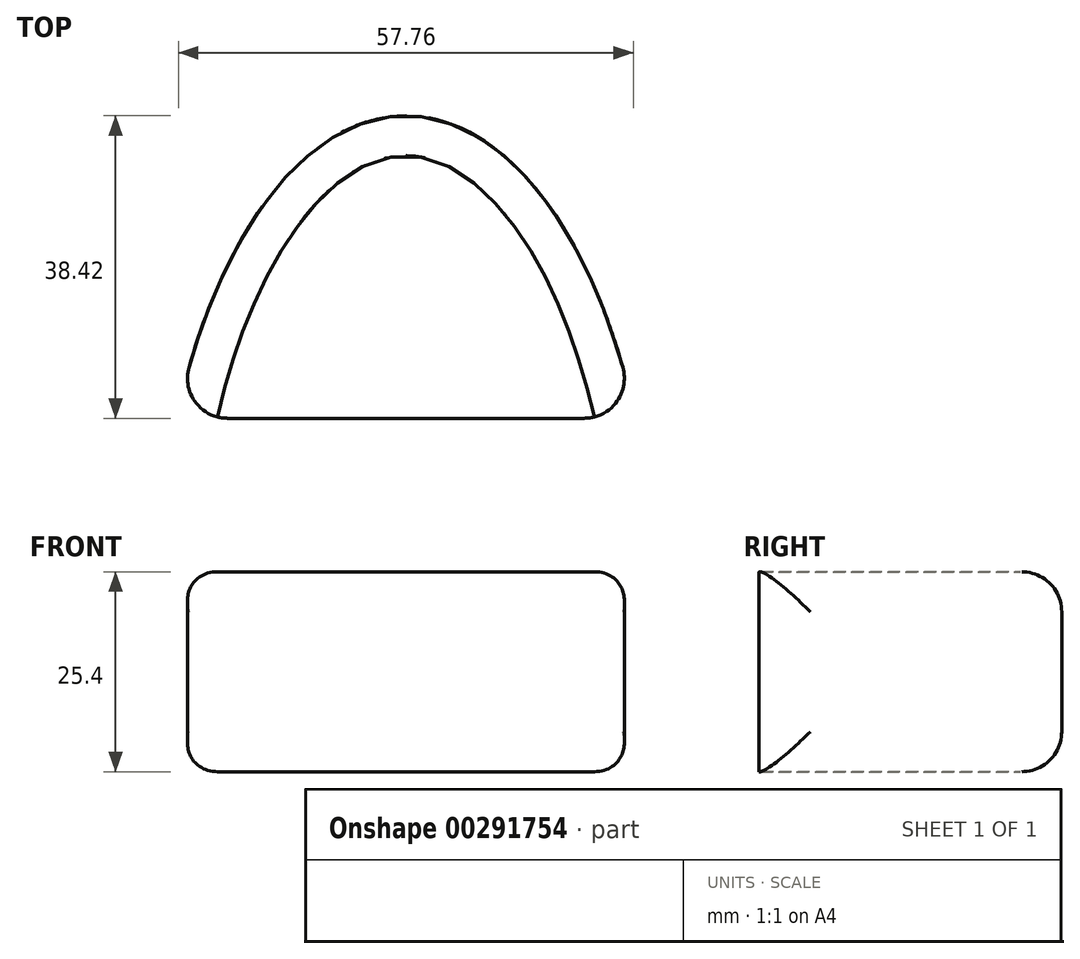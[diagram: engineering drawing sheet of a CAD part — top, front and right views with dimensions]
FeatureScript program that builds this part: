
annotation { "Feature Type Name" : "Feature", "Feature Type Description" : "" }
export const myFeature = defineFeature(function(context is Context, id is Id, definition is map)
    precondition{}
    {
        {
            var Q0;
            Q0=qCreatedBy(makeId("Top.planeOp"),FACE);
            var sketch = newSketch(context, id + "F0", { "sketchPlane" : qUnion([Q0])});
            skEllipticalArc(sketch, "E0", {});
            skFitSpline(sketch, "E1.0", {"points": [v(1.64, 55.77) * mm, v(0, 55.93) * mm, v(-1.64, 55.77) * mm, v(-3.37, 55.26) * mm, v(-5.25, 54.33) * mm, v(-7.27, 52.89) * mm, v(-9.39, 50.9) * mm, v(-11.52, 48.35) * mm, v(-13.28, 45.76) * mm, v(-14.64, 43.41) * mm, v(-15.64, 41.51) * mm, v(-16.6, 39.5) * mm, v(-17.82, 36.66) * mm, v(-19.22, 32.88) * mm, v(-20.69, 27.99) * mm, v(-21.91, 22.8) * mm, v(-22.89, 17.36) * mm, v(-23.6, 11.71) * mm, v(-23.96, 6.88) * mm, v(-24.1, 2.96) * mm, v(-24.14, 0) * mm, v(-24.1, -2.96) * mm, v(-23.96, -6.88) * mm, v(-23.6, -11.71) * mm, v(-22.89, -17.36) * mm, v(-21.91, -22.8) * mm, v(-20.69, -27.99) * mm, v(-19.22, -32.88) * mm, v(-17.82, -36.66) * mm, v(-16.6, -39.5) * mm, v(-15.64, -41.51) * mm, v(-14.64, -43.41) * mm, v(-13.28, -45.76) * mm, v(-11.52, -48.35) * mm, v(-9.39, -50.9) * mm, v(-7.27, -52.89) * mm, v(-5.25, -54.33) * mm, v(-3.37, -55.26) * mm, v(-1.64, -55.77) * mm, v(0, -55.93) * mm, v(1.64, -55.77) * mm, v(3.37, -55.26) * mm, v(5.25, -54.33) * mm, v(7.27, -52.89) * mm, v(9.39, -50.9) * mm, v(11.52, -48.35) * mm, v(13.28, -45.76) * mm, v(14.64, -43.41) * mm, v(15.64, -41.51) * mm, v(16.6, -39.5) * mm, v(17.82, -36.66) * mm, v(19.22, -32.88) * mm, v(20.69, -27.99) * mm, v(21.91, -22.8) * mm, v(22.89, -17.36) * mm, v(23.6, -11.71) * mm, v(23.96, -6.88) * mm, v(24.1, -2.96) * mm, v(24.14, 0) * mm, v(24.1, 2.96) * mm, v(23.96, 6.88) * mm, v(23.6, 11.71) * mm, v(22.89, 17.36) * mm, v(21.91, 22.8) * mm, v(20.69, 27.99) * mm, v(19.22, 32.88) * mm, v(17.82, 36.66) * mm, v(16.6, 39.5) * mm, v(15.64, 41.51) * mm, v(14.64, 43.41) * mm, v(13.28, 45.76) * mm, v(11.52, 48.35) * mm, v(9.39, 50.9) * mm, v(7.27, 52.89) * mm, v(5.25, 54.33) * mm, v(3.37, 55.26) * mm, v(1.64, 55.77) * mm, v(0, 55.93) * mm, v(-1.64, 55.77) * mm]});
            skLineSegment(sketch, "E2", {"start": v(19.72, -31.15) * mm, "end": v(27.67, -31.15) * mm});
            skLineSegment(sketch, "E3", {"start": v(-29.17, 25.08) * mm, "end": v(29.17, 25.08) * mm});
            skLineSegment(sketch, "E4", {"start": v(-22.47, 19.59) * mm, "end": v(-15.64, 25.08) * mm});
            const initialGuessF0  = {"E0": [0, 0, 0, 1, 0.0635, 0.03175, 5.118381350512937, 4.199603077229703]};
            skSetInitialGuess(sketch, initialGuessF0);
            skSolve(sketch);
        }
        {
            var Q0;
            Q0 = qSketchRegion(id + "F0", true);
            extrude(context, id + "F1", {"entities" : qUnion([Q0]), "depth" : 25.4 * mm});
        }
        {
            var Q0;
            Q0=makeQuery(id+"F1.opExtrude","CAP_EDGE",EDGE,{"disambiguationData":[OSD([sQuery(id+"F0.wireOp",EDGE,"E0")])],"isStart":false});
            var Q1;
            Q1=makeQuery(id+"F1.opExtrude","CAP_EDGE",EDGE,{"disambiguationData":[OSD([sQuery(id+"F0.wireOp",EDGE,"E1.0")])],"isStart":false});
            var Q2;
            Q2=makeQuery(id+"F1.opExtrude","SWEPT_FACE",FACE,{"disambiguationData":[OSD([sQuery(id+"F0.wireOp",EDGE,"E1.0")])]});
            var Q3;
            Q3=makeQuery(id+"F1.opExtrude","CAP_EDGE",EDGE,{"disambiguationData":[OSD([sQuery(id+"F0.wireOp",EDGE,"E0")])],"isStart":true});
            var Q4;
            Q4=makeQuery(id+"F1.opExtrude","SWEPT_EDGE",EDGE,{"disambiguationData":[OSD([sQuery(id+"F0.wireOp",EDGE,"E0"),sQuery(id+"F0.wireOp",EDGE,"E3")])]});
            fillet(context, id + "F2", {"entities" : qUnion([Q0, Q1, Q2, Q3, Q4]), "radius" : 5.08 * mm, "tangentPropagation" : true, "allowEdgeOverflow" : false});
        }
    });
